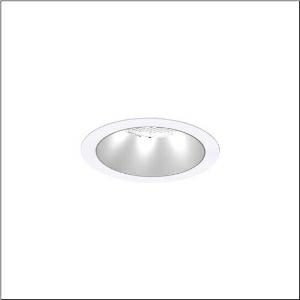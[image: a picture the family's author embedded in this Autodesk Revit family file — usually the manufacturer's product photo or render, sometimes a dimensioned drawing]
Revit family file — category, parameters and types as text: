
# Revit family: lunis_21_l_51db19ed91c
name_source: partatom
category: Lighting Fixtures
units: mm (PartAtom-declared; Revit-internal decimal feet)

## family parameters
Cut with Voids When Loaded = No
Host = Face
Light Source = No
Part Type = Normal
Room Calculation Point = No
Round Connector Dimension = Use Diameter
Shared = No

## types (1)
- --- (1 x LED, 3860 lm, 25.4 W, 6500K)
    Apparent Load = 25 VA
    CIE Flux Codes = 91 99 100 100 100
    Color Rendering = 80
    Color Temperature = 6500K
    Default Elevation = 1800 mm
    Description = Lunis 21,  L, downlight, light control with lens, of PMMA, anti glare with reflector, of PC, matt, light emission: direct distribution, LED rated luminous flux: 2.020lm, light colour: 830/840/865, with terminal, 5-pole, mains connection: 220..240V, AC/DC, 0/50..60Hz, housing, round, of diecast aluminium, traffic white (RAL 9016), diameter: 165mm, clamping range: 1..40mm, protection rating (complete): IP20, protection rating (on room side): IP54, insulation class (complete): insulation class II (safety insulation), certification: CE, impact resistance: IK03, packaging unit: 1 piece
    Height = 0 mm  [stored 0 ft]
    Lamp = 1 x LED
    Lamp Light Flux = 3860 lm
    Lamp Power = 25.4 W
    Lamp count = 1
    Length = 165 mm
    Luminous efficacy = 152 lm/W
    Manufacturer = Siteco
    ModVariant = No
    Model = 51DB19ED91C
    Mounting Place = Ceiling
    Mounting Type = Recessed
    Number of Poles = 1
    OnlyDefault = Yes
    Power Factor = 1
    Product Name = Lunis 21 L
    Product group = downlight
    ProductGroupID = 401
    Protection Class = Protection class II
    Protection Degree = IP 20
    RLX_Detail_Level = 1
    RLX_Emergency_Light_Flux = 0 lm
    RLX_Emergency_Type = 0
    RLX_Emergency_Type_DB = No
    RlxData = <blob elided: 18613 chars, md5=6e8c2c6a>
    Socket = socket
    Standby Power = 0 W
    System Light Flux = 3860 lm
    System Power = 25 W
    Type Comments = individual setting: colour temperature 6500K, luminous flux: 100 % | (ON | ON | OFF | OFF) | 700 mA
    Type Image = l_1291096.jpg
    URL = http://relux.com
    VarID = @adj_038869
    Voltage = 0 V
    Weight = 0.00 kg
    Width = 0 mm  [stored 0 ft]

note: [stored X ft] marks values corroborated as IEEE doubles in the binary element streams (Revit-internal decimal feet)

## geometry (parser evidence)
native form markers: Blend x4, Sweep x9
no freeform markers — native parametric forms only
